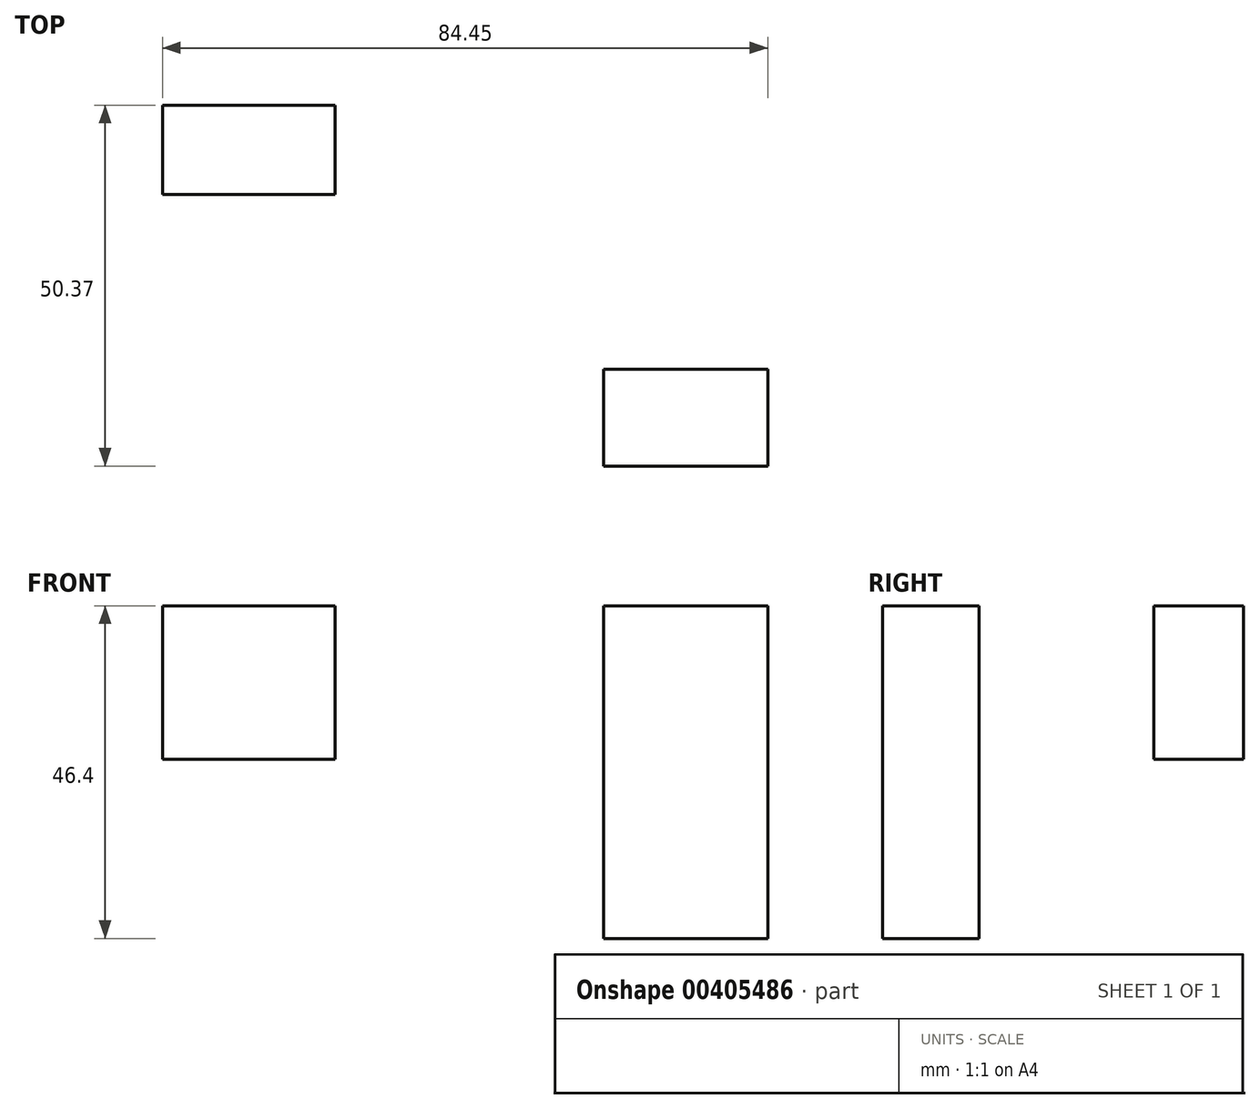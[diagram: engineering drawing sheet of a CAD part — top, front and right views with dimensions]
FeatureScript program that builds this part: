
annotation { "Feature Type Name" : "Feature", "Feature Type Description" : "" }
export const myFeature = defineFeature(function(context is Context, id is Id, definition is map)
    precondition{}
    {
        {
            var Q0;
            Q0=qCreatedBy(makeId("Top.planeOp"),FACE);
            var sketch = newSketch(context, id + "F0", { "sketchPlane" : qUnion([Q0])});
            skLineSegment(sketch, "E0.bottom", {"start": v(-40.5, 23.95) * mm, "end": v(43.95, 23.95) * mm});
            skLineSegment(sketch, "E0.top", {"start": v(-40.5, -26.42) * mm, "end": v(43.95, -26.42) * mm});
            skLineSegment(sketch, "E0.left", {"start": v(-40.5, 23.95) * mm, "end": v(-40.5, -26.42) * mm});
            skLineSegment(sketch, "E0.right", {"start": v(43.95, 23.95) * mm, "end": v(43.95, -26.42) * mm});
            skLineSegment(sketch, "E1.bottom", {"start": v(10.2, -7.33) * mm, "end": v(-10.2, -7.33) * mm});
            skLineSegment(sketch, "E1.top", {"start": v(10.2, 7.33) * mm, "end": v(-10.2, 7.33) * mm});
            skLineSegment(sketch, "E1.left", {"start": v(10.2, -7.33) * mm, "end": v(10.2, 7.33) * mm});
            skLineSegment(sketch, "E1.right", {"start": v(-10.2, -7.33) * mm, "end": v(-10.2, 7.33) * mm});
            skPoint(sketch, "E1.middle", {"position": v(0, 0) * mm});
            skLineSegment(sketch, "E2.bottom", {"start": v(-40.5, 23.95) * mm, "end": v(-16.42, 23.95) * mm});
            skLineSegment(sketch, "E2.top", {"start": v(-40.5, 11.48) * mm, "end": v(-16.42, 11.48) * mm});
            skLineSegment(sketch, "E2.left", {"start": v(-40.5, 23.95) * mm, "end": v(-40.5, 11.48) * mm});
            skLineSegment(sketch, "E2.right", {"start": v(-16.42, 23.95) * mm, "end": v(-16.42, 11.48) * mm});
            skLineSegment(sketch, "E3.bottom", {"start": v(43.95, -12.91) * mm, "end": v(21.04, -12.91) * mm});
            skLineSegment(sketch, "E3.top", {"start": v(43.95, -26.42) * mm, "end": v(21.04, -26.42) * mm});
            skLineSegment(sketch, "E3.left", {"start": v(43.95, -12.91) * mm, "end": v(43.95, -26.42) * mm});
            skLineSegment(sketch, "E3.right", {"start": v(21.04, -12.91) * mm, "end": v(21.04, -26.42) * mm});
            skSolve(sketch);
        }
        {
            var Q0;
            Q0=makeQuery(id+"F0.imprint","IMPRINT",FACE,{"disambiguationData":[TD([[makeQuery(id+"F0.imprint","IMPRINT",EDGE,{"derivedFrom":sQuery(id+"F0.wireOp",EDGE,"E2.bottom")}),-1.0]])]});
            var Q1;
            Q1=makeQuery(id+"F0.imprint","IMPRINT",FACE,{"disambiguationData":[TD([[makeQuery(id+"F0.imprint","IMPRINT",EDGE,{"derivedFrom":sQuery(id+"F0.wireOp",EDGE,"E3.bottom")}),1.0]])]});
            var Q2;
            Q2=makeQuery(id+"F0.imprint","IMPRINT",FACE,{"disambiguationData":[TD([[makeQuery(id+"F0.imprint","IMPRINT",EDGE,{"derivedFrom":sQuery(id+"F0.wireOp",EDGE,"E0.bottom")}),-1.0]])]});
            extrude(context, id + "F1", {"entities" : qUnion([Q0, Q1, Q2]), "depth" : 46.4 * mm});
        }
        {
            var Q0;
            Q0=makeQuery(id+"F0.imprint","IMPRINT",FACE,{"disambiguationData":[TD([[makeQuery(id+"F0.imprint","IMPRINT",EDGE,{"derivedFrom":sQuery(id+"F0.wireOp",EDGE,"E0.bottom")}),-1.0]])]});
            extrude(context, id + "F2", {"entities" : qUnion([Q0]), "operationType" : NewBodyOperationType.REMOVE, "depth" : 25 * mm});
        }
    });
